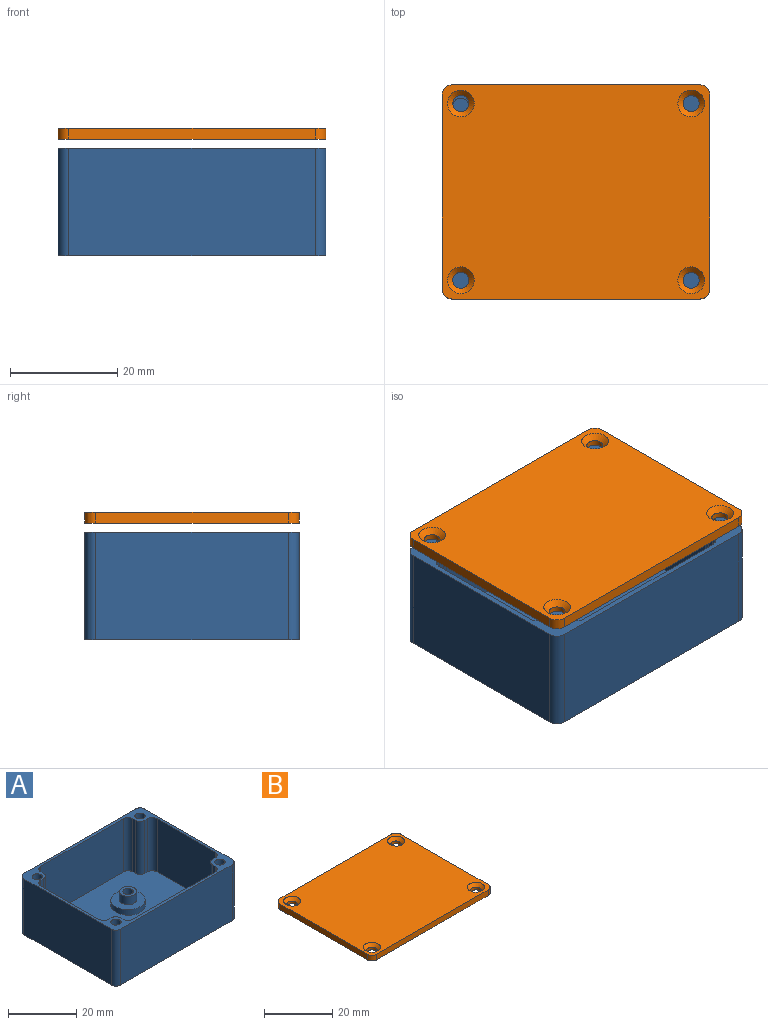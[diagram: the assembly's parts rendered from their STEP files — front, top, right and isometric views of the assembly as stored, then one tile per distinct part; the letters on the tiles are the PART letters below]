
ASSEMBLY  parts=2 mates=1
PART A: 67 faces, bbox 50x40x20 mm
  f0: cylinder r=1.5mm len=4mm, axis (0,0,-1), area 37.7mm2, adj f30,f50
  f1: cylinder r=1.5mm len=4mm, axis (0,0,-1), area 37.7mm2, adj f32,f43
  f2: plane 48x38mm, normal (0,0,1), area 1563.5mm2, adj f3,f4,f5,f6,f13,f14,f15,f16
  f3: plane 34x19mm, normal (0,1,0), area 646mm2, adj f2,f7,f55,f59
  f4: plane 24x19mm, normal (-1,0,0), area 456mm2, adj f2,f7,f57,f62
  f5: plane 24x19mm, normal (1,0,0), area 456mm2, adj f2,f7,f53,f56
  f6: plane 34x19mm, normal (0,-1,0), area 646mm2, adj f2,f7,f51,f61
  f7: plane 50x40mm, normal (0,0,1), area 247.7mm2, adj f3,f4,f5,f6,f8,f9,f10,f11
  f8: plane 46x20mm, normal (0,1,0), area 920mm2, adj f7,f12,f63,f66
  f9: plane 36x20mm, normal (-1,0,0), area 720mm2, adj f7,f12,f63,f64
  f10: plane 46x20mm, normal (0,-1,0), area 920mm2, adj f7,f12,f64,f65
  f11: plane 36x20mm, normal (1,0,0), area 720mm2, adj f7,f12,f65,f66
  f12: plane 50x40mm, normal (0,0,-1), area 1949.8mm2, adj f8,f9,f10,f11,f37,f38,f39,f40
  f13: plane 19x1mm, normal (0,-1,0), area 19mm2, adj f2,f7,f52,f53
  f14: plane 19x1mm, normal (1,0,0), area 19mm2, adj f2,f7,f51,f52
  f15: plane 19x1mm, normal (0,-1,0), area 19mm2, adj f2,f7,f60,f62
  f16: plane 19x1mm, normal (-1,0,0), area 19mm2, adj f2,f7,f60,f61
  f17: plane 19x1mm, normal (0,1,0), area 19mm2, adj f2,f7,f54,f56
  f18: plane 19x1mm, normal (1,0,0), area 19mm2, adj f2,f7,f54,f55
  f19: plane 19x1mm, normal (0,1,0), area 19mm2, adj f2,f7,f57,f58
  f20: plane 19x1mm, normal (-1,0,0), area 19mm2, adj f2,f7,f58,f59
  f21: cylinder r=1.5mm len=10mm, axis (0,0,1), area 94.2mm2, adj f7,f22
  f22: plane 3x3mm, normal (0,0,1), area 7.1mm2, adj f21
  f23: cylinder r=1.5mm len=10mm, axis (0,0,1), area 94.2mm2, adj f7,f24
  f24: plane 3x3mm, normal (0,0,1), area 7.1mm2, adj f23
  f25: cylinder r=1.5mm len=10mm, axis (0,0,1), area 94.2mm2, adj f7,f26
  f26: plane 3x3mm, normal (0,0,1), area 7.1mm2, adj f25
  f27: cylinder r=1.5mm len=10mm, axis (0,0,1), area 94.2mm2, adj f7,f28
  f28: plane 3x3mm, normal (0,0,1), area 7.1mm2, adj f27
  f29: cylinder r=2.5mm len=5mm, axis (0,0,-1), area 47.1mm2, adj f30,f34
  f30: plane 5x5mm, normal (0,0,1), area 12.6mm2, adj f0,f29
  f31: cylinder r=2.5mm len=5mm, axis (0,0,-1), area 47.1mm2, adj f32,f36
  f32: plane 5x5mm, normal (0,0,1), area 12.6mm2, adj f1,f31
  f33: cylinder r=5mm len=10mm, axis (0,0,-1), area 62.8mm2, adj f2,f34
  f34: plane 10x10mm, normal (0,0,1), area 58.9mm2, adj f29,f33
  f35: cylinder r=5mm len=10mm, axis (0,0,-1), area 62.8mm2, adj f2,f36
  f36: plane 10x10mm, normal (0,0,1), area 58.9mm2, adj f31,f35
  f37: plane 2.98x2mm, normal (0.99,-0.12,0), area 6mm2, adj f12,f38,f42,f43
  f38: plane 2.76x2mm, normal (0.39,-0.92,0), area 6mm2, adj f12,f37,f39,f43
  f39: plane 2.4x2mm, normal (-0.6,-0.8,0), area 6mm2, adj f12,f38,f40,f43
  f40: plane 2.98x2mm, normal (-0.99,0.12,0), area 6mm2, adj f12,f39,f41,f43
  f41: plane 2.76x2mm, normal (-0.39,0.92,0), area 6mm2, adj f12,f40,f42,f43
  f42: plane 2.4x2mm, normal (0.6,0.8,0), area 6mm2, adj f12,f37,f41,f43
  f43: plane 5.96x5.52mm, normal (0,0,-1), area 16.3mm2, adj f1,f37,f38,f39,f40,f41,f42
  f44: plane 2.7x2mm, normal (0.9,-0.43,0), area 6mm2, adj f12,f45,f49,f50
  f45: plane 2.99x2mm, normal (0.08,-1,0), area 6mm2, adj f12,f44,f46,f50
  f46: plane 2.48x2mm, normal (-0.83,-0.56,0), area 6mm2, adj f12,f45,f47,f50
  f47: plane 2.7x2mm, normal (-0.9,0.43,0), area 6mm2, adj f12,f46,f48,f50
  f48: plane 2.99x2mm, normal (-0.08,1,0), area 6mm2, adj f12,f47,f49,f50
  f49: plane 2.48x2mm, normal (0.83,0.56,0), area 6mm2, adj f12,f44,f48,f50
  f50: plane 5.98x5.41mm, normal (0,0,-1), area 16.3mm2, adj f0,f44,f45,f46,f47,f48,f49
  f51: cylinder r=2mm len=19mm, axis (0,0,-1), area 59.7mm2, adj f2,f6,f7,f14
  f52: cylinder r=2mm len=19mm, axis (0,0,1), area 59.7mm2, adj f2,f7,f13,f14
  f53: cylinder r=2mm len=19mm, axis (0,0,-1), area 59.7mm2, adj f2,f5,f7,f13
  f54: cylinder r=2mm len=19mm, axis (0,0,1), area 59.7mm2, adj f2,f7,f17,f18
  f55: cylinder r=2mm len=19mm, axis (0,0,-1), area 59.7mm2, adj f2,f3,f7,f18
  f56: cylinder r=2mm len=19mm, axis (0,0,1), area 59.7mm2, adj f2,f5,f7,f17
  f57: cylinder r=2mm len=19mm, axis (0,0,1), area 59.7mm2, adj f2,f4,f7,f19
  f58: cylinder r=2mm len=19mm, axis (0,0,1), area 59.7mm2, adj f2,f7,f19,f20
  f59: cylinder r=2mm len=19mm, axis (0,0,1), area 59.7mm2, adj f2,f3,f7,f20
  f60: cylinder r=2mm len=19mm, axis (0,0,1), area 59.7mm2, adj f2,f7,f15,f16
  f61: cylinder r=2mm len=19mm, axis (0,0,1), area 59.7mm2, adj f2,f6,f7,f16
  f62: cylinder r=2mm len=19mm, axis (0,0,-1), area 59.7mm2, adj f2,f4,f7,f15
  f63: cylinder r=2mm len=20mm, axis (0,0,1), area 62.8mm2, adj f7,f8,f9,f12
  f64: cylinder r=2mm len=20mm, axis (0,0,-1), area 62.8mm2, adj f7,f9,f10,f12
  f65: cylinder r=2mm len=20mm, axis (0,0,1), area 62.8mm2, adj f7,f10,f11,f12
  f66: cylinder r=2mm len=20mm, axis (0,0,-1), area 62.8mm2, adj f7,f8,f11,f12
PART B: 18 faces, bbox 50x40x2 mm
  f0: plane 36x2mm, normal (1,0,0), area 72mm2, adj f4,f5,f14,f17
  f1: plane 46x2mm, normal (0,1,0), area 92mm2, adj f4,f5,f14,f15
  f2: plane 36x2mm, normal (-1,0,0), area 72mm2, adj f4,f5,f15,f16
  f3: plane 46x2mm, normal (0,-1,0), area 92mm2, adj f4,f5,f16,f17
  f4: plane 50x40mm, normal (0,0,1), area 1918mm2, adj f0,f1,f2,f3,f10,f11,f12,f13
  f5: plane 50x40mm, normal (0,0,-1), area 1968.3mm2, adj f0,f1,f2,f3,f6,f7,f8,f9
  f6: cylinder r=1.5mm len=3mm, axis (0,0,1), area 9.4mm2, adj f5,f11
  f7: cylinder r=1.5mm len=3mm, axis (0,0,1), area 9.4mm2, adj f5,f12
  f8: cylinder r=1.5mm len=3mm, axis (0,0,1), area 9.4mm2, adj f5,f13
  f9: cylinder r=1.5mm len=3mm, axis (0,0,1), area 9.4mm2, adj f5,f10
  f10: cone r=1.5mm half-angle=45deg, axis (0,0,1), area 17.8mm2, adj f4,f9
  f11: cone r=1.5mm half-angle=45deg, axis (0,0,1), area 17.8mm2, adj f4,f6
  f12: cone r=1.5mm half-angle=45deg, axis (0,0,1), area 17.8mm2, adj f4,f7
  f13: cone r=1.5mm half-angle=45deg, axis (0,0,1), area 17.8mm2, adj f4,f8
  f14: cylinder r=2mm len=2mm, axis (0,0,1), area 6.3mm2, adj f0,f1,f4,f5
  f15: cylinder r=2mm len=2mm, axis (0,0,-1), area 6.3mm2, adj f1,f2,f4,f5
  f16: cylinder r=2mm len=2mm, axis (0,0,1), area 6.3mm2, adj f2,f3,f4,f5
  f17: cylinder r=2mm len=2mm, axis (0,0,-1), area 6.3mm2, adj f0,f3,f4,f5
PLACE A t=(-54.37,-36.55,-7.73)mm fixed
PLACE B t=(-46.38,25.97,13.99)mm
MATE slider A.f23 <-> B.f6  axis (0,0,1) through (-67.42,-13.02,12.27)mm
